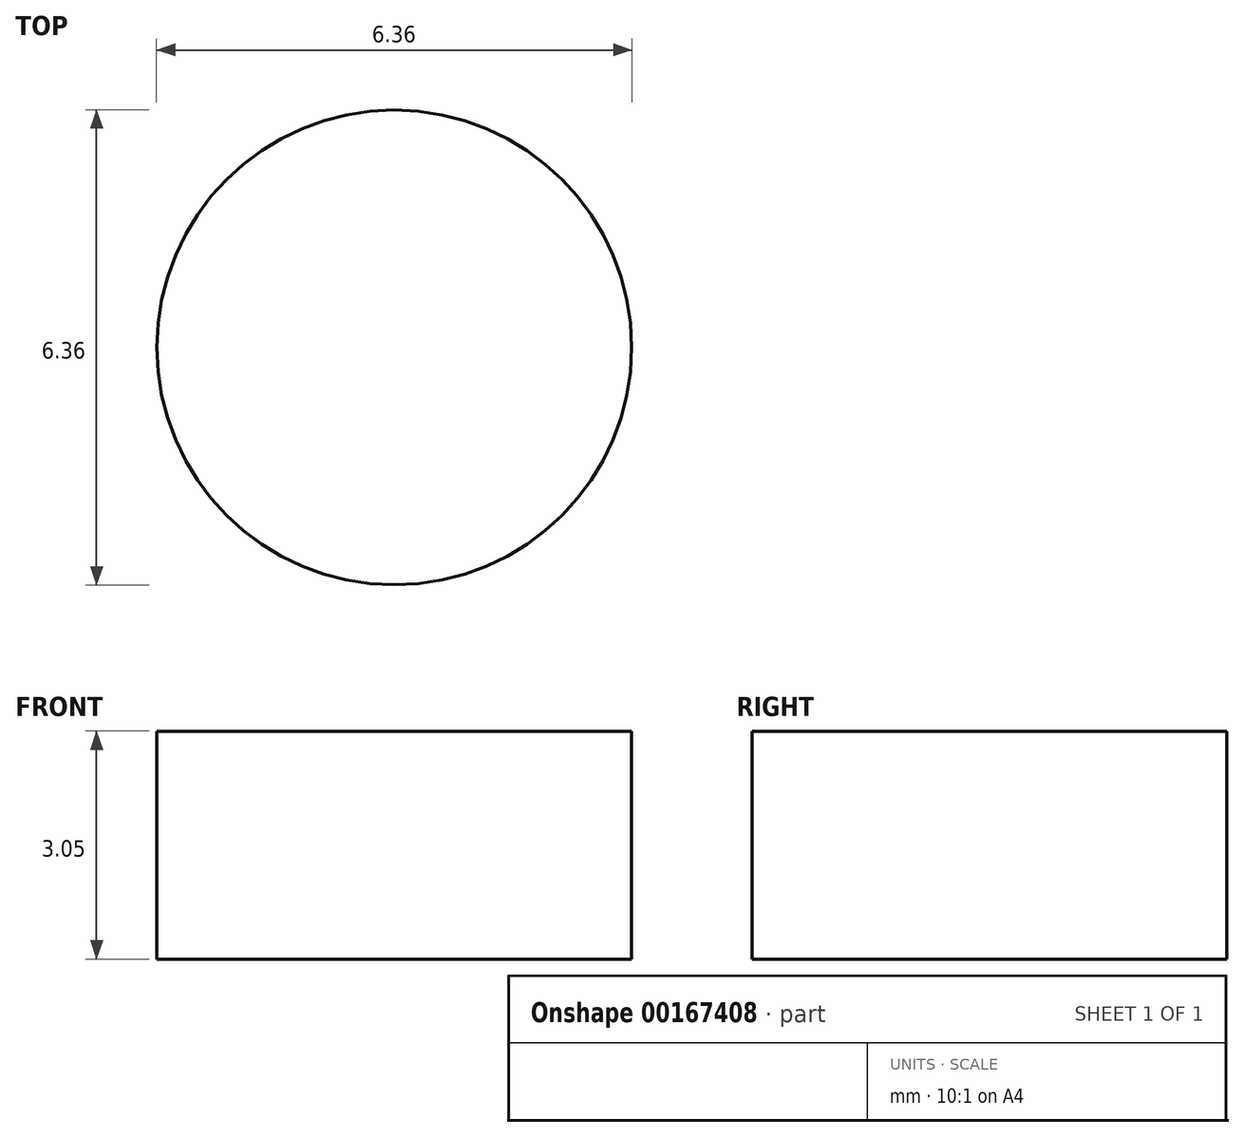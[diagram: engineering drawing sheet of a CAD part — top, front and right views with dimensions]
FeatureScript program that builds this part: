
annotation { "Feature Type Name" : "Feature", "Feature Type Description" : "" }
export const myFeature = defineFeature(function(context is Context, id is Id, definition is map)
    precondition{}
    {
        {
            var Q0;
            Q0=qCreatedBy(makeId("Top.planeOp"),FACE);
            var sketch = newSketch(context, id + "F0", { "sketchPlane" : qUnion([Q0])});
            skCircle(sketch, "E0", {"center": v(0, 0) * mm, "radius": 3.18 * mm});
            skSolve(sketch);
        }
        {
            var Q0;
            Q0=makeQuery(id+"F0.imprint","IMPRINT",FACE,{"disambiguationData":[TD([[makeQuery(id+"F0.imprint","IMPRINT",EDGE,{"derivedFrom":sQuery(id+"F0.wireOp",EDGE,"E0")}),1.0]])]});
            extrude(context, id + "F1", {"entities" : qUnion([Q0]), "depth" : 3.05 * mm});
        }
    });
